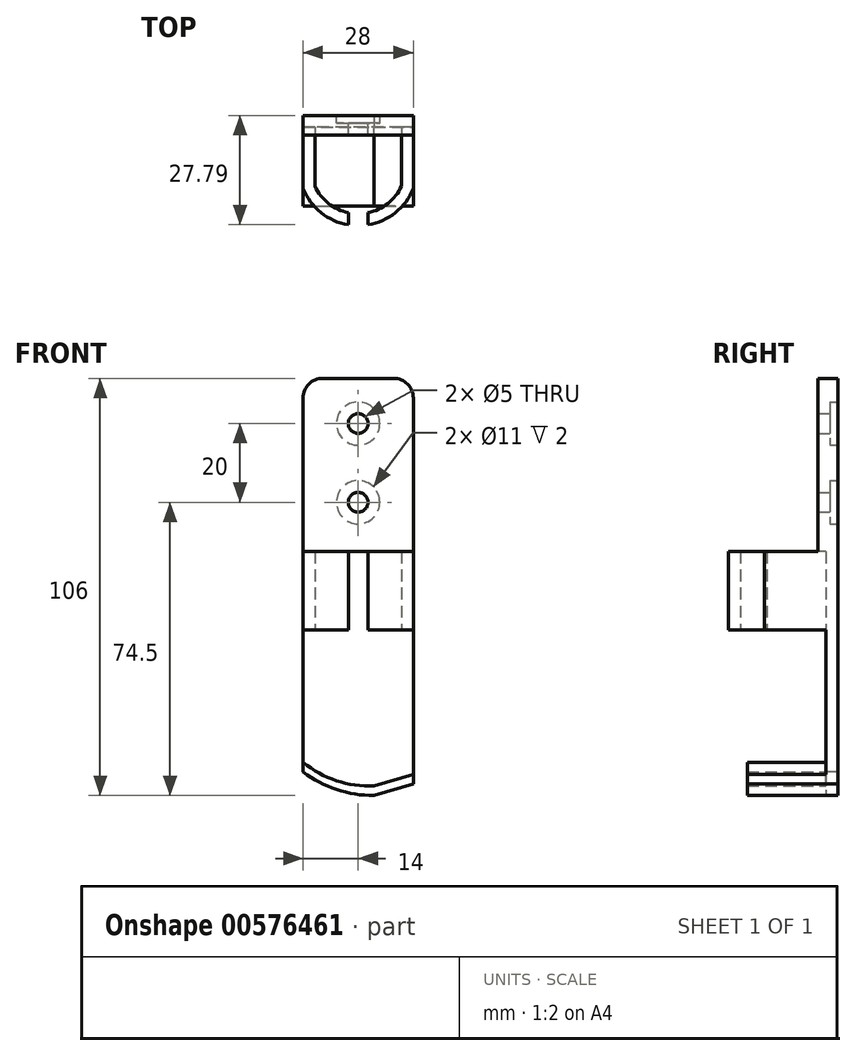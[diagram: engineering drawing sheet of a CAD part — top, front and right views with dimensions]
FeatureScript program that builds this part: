
annotation { "Feature Type Name" : "Feature", "Feature Type Description" : "" }
export const myFeature = defineFeature(function(context is Context, id is Id, definition is map)
    precondition{}
    {
        {
            var Q0;
            Q0=qCreatedBy(makeId("Top.planeOp"),FACE);
            var sketch = newSketch(context, id + "F0", { "sketchPlane" : qUnion([Q0])});
            skLineSegment(sketch, "E0.bottom", {"start": v(11, 11) * mm, "end": v(-11, 11) * mm});
            skLineSegment(sketch, "E0.left", {"start": v(11, 11) * mm, "end": v(11, -3.98) * mm});
            skLineSegment(sketch, "E0.right", {"start": v(-11, 11) * mm, "end": v(-11, -3.98) * mm});
            skPoint(sketch, "E0.middle", {"position": v(0, 0) * mm});
            skArc(sketch, "E1", {"start": v(-11, -3.98) * mm, "mid": v(0, -11) * mm, "end": v(11, -3.98) * mm});
            skPoint(sketch, "E2.orphan", {"position": v(-11, -11) * mm});
            skPoint(sketch, "E0.top.start.orphan", {"position": v(11, -11) * mm});
            skLineSegment(sketch, "E3.0", {"start": v(14, 14) * mm, "end": v(-14, 14) * mm});
            skLineSegment(sketch, "E3.1", {"start": v(14, 14) * mm, "end": v(14, -4.6) * mm});
            skArc(sketch, "E3.2", {"start": v(-14, -4.6) * mm, "mid": v(0, -14) * mm, "end": v(14, -4.6) * mm});
            skLineSegment(sketch, "E3.3", {"start": v(-14, 14) * mm, "end": v(-14, -4.6) * mm});
            skSolve(sketch);
        }
        {
            var Q0;
            Q0=makeQuery(id+"F0.imprint","IMPRINT",FACE,{"disambiguationData":[TD([[makeQuery(id+"F0.imprint","IMPRINT",EDGE,{"derivedFrom":sQuery(id+"F0.wireOp",EDGE,"E0.bottom")}),-1.0]])]});
            extrude(context, id + "F1", {"entities" : qUnion([Q0]), "depth" : 20 * mm, "offsetDistance" : 25 * mm});
        }
        {
            var Q0;
            Q0=makeQuery(id+"F1.opExtrude","CAP_FACE",FACE,{"disambiguationData":[OSD([sQuery(id+"F0.wireOp",EDGE,"E0.bottom"),sQuery(id+"F0.wireOp",EDGE,"E0.left"),sQuery(id+"F0.wireOp",EDGE,"E0.right"),sQuery(id+"F0.wireOp",EDGE,"E1"),sQuery(id+"F0.wireOp",EDGE,"E3.0"),sQuery(id+"F0.wireOp",EDGE,"E3.1"),sQuery(id+"F0.wireOp",EDGE,"E3.2"),sQuery(id+"F0.wireOp",EDGE,"E3.3")])],"isStart":false});
            var sketch = newSketch(context, id + "F2", { "sketchPlane" : qUnion([Q0])});
            skLineSegment(sketch, "E4.bottom", {"start": v(-14, 14) * mm, "end": v(14, 14) * mm});
            skLineSegment(sketch, "E4.top", {"start": v(-14, 9) * mm, "end": v(14, 9) * mm});
            skLineSegment(sketch, "E4.left", {"start": v(-14, 14) * mm, "end": v(-14, 9) * mm});
            skLineSegment(sketch, "E4.right", {"start": v(14, 14) * mm, "end": v(14, 9) * mm});
            skSolve(sketch);
        }
        {
            var Q0;
            Q0=makeQuery(id+"F2.imprint","IMPRINT",FACE,{"disambiguationData":[TD([[makeQuery(id+"F2.imprint","IMPRINT",EDGE,{"derivedFrom":sQuery(id+"F2.wireOp",EDGE,"E4.bottom")}),1.0]])]});
            var Q1;
            {var subQ5=makeQuery(id+"F1.opExtrude","CAP_EDGE",EDGE,{"disambiguationData":[OSD([sQuery(id+"F0.wireOp",EDGE,"E0.bottom")])],"isStart":false});Q1=makeQuery(id+"F2.imprint","IMPRINT",FACE,{"disambiguationData":[TD([[makeQuery(id+"F2.imprint","IMPRINT",EDGE,{"derivedFrom":subQ5}),1.0]])]});}
            var Q2;
            Q2 = qSketchRegion(id + "F4", true);
            extrude(context, id + "F3", {"entities" : qUnion([Q0, Q1, Q2]), "operationType" : NewBodyOperationType.ADD, "depth" : 44 * mm, "offsetDistance" : 25 * mm});
        }
        {
            var Q0;
            Q0=makeQuery(id+"F3.boolean.opBoolean","MERGE",FACE,{"derivedFrom":[makeQuery(id+"F1.opExtrude","SWEPT_FACE",FACE,{"disambiguationData":[OSD([sQuery(id+"F0.wireOp",EDGE,"E3.0")])]}),makeQuery(id+"F3.opExtrude","SWEPT_FACE",FACE,{"disambiguationData":[OSD([sQuery(id+"F2.wireOp",EDGE,"E4.bottom")])]})]});
            var sketch = newSketch(context, id + "F4", { "sketchPlane" : qUnion([Q0])});
            skCircle(sketch, "E5", {"center": v(0, 52.5) * mm, "radius": 5.5 * mm});
            skPoint(sketch, "E5.centerSnap0", {"position": v(0, 64) * mm});
            skCircle(sketch, "E6", {"center": v(0, 32.5) * mm, "radius": 5.5 * mm});
            skSolve(sketch);
        }
        {
            var Q0;
            Q0=sQuery(id+"F4.wireOp",VERTEX,"E5.center");
            var Q1;
            Q1=sQuery(id+"F4.wireOp",VERTEX,"E6.center");
            var Q2;
            Q2=makeQuery(id+"F1.opExtrude","SWEPT_BODY",BODY,{"disambiguationData":[OSD([sQuery(id+"F0.wireOp",EDGE,"E0.bottom"),sQuery(id+"F0.wireOp",EDGE,"E0.left"),sQuery(id+"F0.wireOp",EDGE,"E0.right"),sQuery(id+"F0.wireOp",EDGE,"E1"),sQuery(id+"F0.wireOp",EDGE,"E3.0"),sQuery(id+"F0.wireOp",EDGE,"E3.1"),sQuery(id+"F0.wireOp",EDGE,"E3.2"),sQuery(id+"F0.wireOp",EDGE,"E3.3")])]});
            hole(context, id + "F5", {"style" : HoleStyle.C_BORE, "endStyle" : HoleEndStyle.THROUGH, "holeDiameter" : 5 * mm, "cBoreDiameter" : 11 * mm, "cBoreDepth" : 2 * mm, "isTappedThrough" : true, "tappedDepth" : 12 * mm, "tapClearance" : 3, "locations" : qUnion([Q0, Q1]), "scope" : qUnion([Q2])});
        }
        {
            var Q0;
            Q0=makeQuery(id+"F3.opExtrude","CAP_EDGE",EDGE,{"disambiguationData":[OSD([sQuery(id+"F2.wireOp",EDGE,"E4.left")])],"isStart":false});
            var Q1;
            Q1=makeQuery(id+"F3.opExtrude","CAP_EDGE",EDGE,{"disambiguationData":[OSD([sQuery(id+"F2.wireOp",EDGE,"E4.right")])],"isStart":false});
            fillet(context, id + "F6", {"entities" : qUnion([Q0, Q1]), "radius" : 5 * mm, "tangentPropagation" : true, "allowEdgeOverflow" : false});
        }
        {
            var Q0;
            Q0=makeQuery(id+"F1.opExtrude","CAP_FACE",FACE,{"disambiguationData":[OSD([sQuery(id+"F0.wireOp",EDGE,"E0.bottom"),sQuery(id+"F0.wireOp",EDGE,"E0.left"),sQuery(id+"F0.wireOp",EDGE,"E0.right"),sQuery(id+"F0.wireOp",EDGE,"E1"),sQuery(id+"F0.wireOp",EDGE,"E3.0"),sQuery(id+"F0.wireOp",EDGE,"E3.1"),sQuery(id+"F0.wireOp",EDGE,"E3.2"),sQuery(id+"F0.wireOp",EDGE,"E3.3")])],"isStart":true});
            var sketch = newSketch(context, id + "F7", { "sketchPlane" : qUnion([Q0])});
            skLineSegment(sketch, "E7.bottom", {"start": v(14, -14) * mm, "end": v(-14, -14) * mm});
            skLineSegment(sketch, "E7.top", {"start": v(14, -11) * mm, "end": v(-14, -11) * mm});
            skLineSegment(sketch, "E7.left", {"start": v(14, -14) * mm, "end": v(14, -11) * mm});
            skLineSegment(sketch, "E7.right", {"start": v(-14, -14) * mm, "end": v(-14, -11) * mm});
            skSolve(sketch);
        }
        {
            var Q0;
            Q0=makeQuery(id+"F7.imprint","IMPRINT",FACE,{"disambiguationData":[TD([[makeQuery(id+"F7.imprint","IMPRINT",EDGE,{"derivedFrom":sQuery(id+"F7.wireOp",EDGE,"E7.bottom")}),-1.0]])]});
            extrude(context, id + "F8", {"entities" : qUnion([Q0]), "operationType" : NewBodyOperationType.ADD, "depth" : 42 * mm, "offsetDistance" : 25 * mm});
        }
        {
            var Q0;
            Q0=makeQuery(id+"F1.opExtrude","CAP_FACE",FACE,{"disambiguationData":[OSD([sQuery(id+"F0.wireOp",EDGE,"E0.bottom"),sQuery(id+"F0.wireOp",EDGE,"E0.left"),sQuery(id+"F0.wireOp",EDGE,"E0.right"),sQuery(id+"F0.wireOp",EDGE,"E1"),sQuery(id+"F0.wireOp",EDGE,"E3.0"),sQuery(id+"F0.wireOp",EDGE,"E3.1"),sQuery(id+"F0.wireOp",EDGE,"E3.2"),sQuery(id+"F0.wireOp",EDGE,"E3.3")])],"isStart":true});
            var sketch = newSketch(context, id + "F9", { "sketchPlane" : qUnion([Q0])});
            skLineSegment(sketch, "E8.bottom", {"start": v(2.5, 8.98) * mm, "end": v(-2.5, 8.98) * mm});
            skLineSegment(sketch, "E8.top", {"start": v(2.5, 19.02) * mm, "end": v(-2.5, 19.02) * mm});
            skLineSegment(sketch, "E8.left", {"start": v(2.5, 8.98) * mm, "end": v(2.5, 19.02) * mm});
            skLineSegment(sketch, "E8.right", {"start": v(-2.5, 8.98) * mm, "end": v(-2.5, 19.02) * mm});
            skPoint(sketch, "E8.middle", {"position": v(0, 14) * mm});
            skSolve(sketch);
        }
        {
            var Q0;
            Q0 = qSketchRegion(id + "F9", true);
            extrude(context, id + "F10", {"entities" : qUnion([Q0]), "operationType" : NewBodyOperationType.REMOVE, "oppositeDirection" : true, "depth" : 20 * mm, "offsetDistance" : 25 * mm});
        }
        {
            var Q0;
            Q0=makeQuery(id+"F8.boolean.opBoolean","MERGE",FACE,{"derivedFrom":[makeQuery(id+"F1.opExtrude","SWEPT_FACE",FACE,{"disambiguationData":[OSD([sQuery(id+"F0.wireOp",EDGE,"E0.bottom")])]}),makeQuery(id+"F8.opExtrude","SWEPT_FACE",FACE,{"disambiguationData":[OSD([sQuery(id+"F7.wireOp",EDGE,"E7.top")])]})]});
            var sketch = newSketch(context, id + "F11", { "sketchPlane" : qUnion([Q0])});
            skLineSegment(sketch, "E9", {"start": v(14, -39) * mm, "end": v(4, -42) * mm});
            skArc(sketch, "E10", {"start": v(-14, -36) * mm, "mid": v(-5.49, -40.46) * mm, "end": v(4, -42) * mm});
            skLineSegment(sketch, "E11", {"start": v(14, -39) * mm, "end": v(19.27, -45.9) * mm});
            skLineSegment(sketch, "E12", {"start": v(19.27, -45.9) * mm, "end": v(-17.4, -47.1) * mm});
            skLineSegment(sketch, "E13", {"start": v(-17.4, -47.1) * mm, "end": v(-17.93, -31.25) * mm});
            skLineSegment(sketch, "E14", {"start": v(-17.93, -31.25) * mm, "end": v(-14, -36) * mm});
            skSolve(sketch);
        }
        {
            var Q0;
            Q0 = qSketchRegion(id + "F11", true);
            extrude(context, id + "F12", {"entities" : qUnion([Q0]), "operationType" : NewBodyOperationType.REMOVE, "oppositeDirection" : true, "depth" : 25 * mm, "offsetDistance" : 25 * mm});
        }
        {
            var Q0;
            Q0=makeQuery(id+"F8.boolean.opBoolean","MERGE",FACE,{"derivedFrom":[makeQuery(id+"F1.opExtrude","SWEPT_FACE",FACE,{"disambiguationData":[OSD([sQuery(id+"F0.wireOp",EDGE,"E0.bottom")])]}),makeQuery(id+"F8.opExtrude","SWEPT_FACE",FACE,{"disambiguationData":[OSD([sQuery(id+"F7.wireOp",EDGE,"E7.top")])]})]});
            var sketch = newSketch(context, id + "F13", { "sketchPlane" : qUnion([Q0])});
            skLineSegment(sketch, "E15", {"start": v(4, -39.6) * mm, "end": v(14, -36.6) * mm});
            skArc(sketch, "E16", {"start": v(-14, -33.6) * mm, "mid": v(-5.55, -38.24) * mm, "end": v(4, -39.6) * mm});
            skLineSegment(sketch, "E17", {"start": v(14, -39) * mm, "end": v(4, -42) * mm});
            skArc(sketch, "E18", {"start": v(-14, -36) * mm, "mid": v(-5.5, -40.48) * mm, "end": v(4, -42) * mm});
            skLineSegment(sketch, "E19", {"start": v(14, -39) * mm, "end": v(14, -36.6) * mm});
            skLineSegment(sketch, "E20", {"start": v(-14, -36) * mm, "end": v(-14, -33.6) * mm});
            skSolve(sketch);
        }
        {
            var Q0;
            Q0 = qSketchRegion(id + "F13", true);
            extrude(context, id + "F14", {"entities" : qUnion([Q0]), "operationType" : NewBodyOperationType.ADD, "depth" : 20 * mm, "offsetDistance" : 25 * mm});
        }
    });
